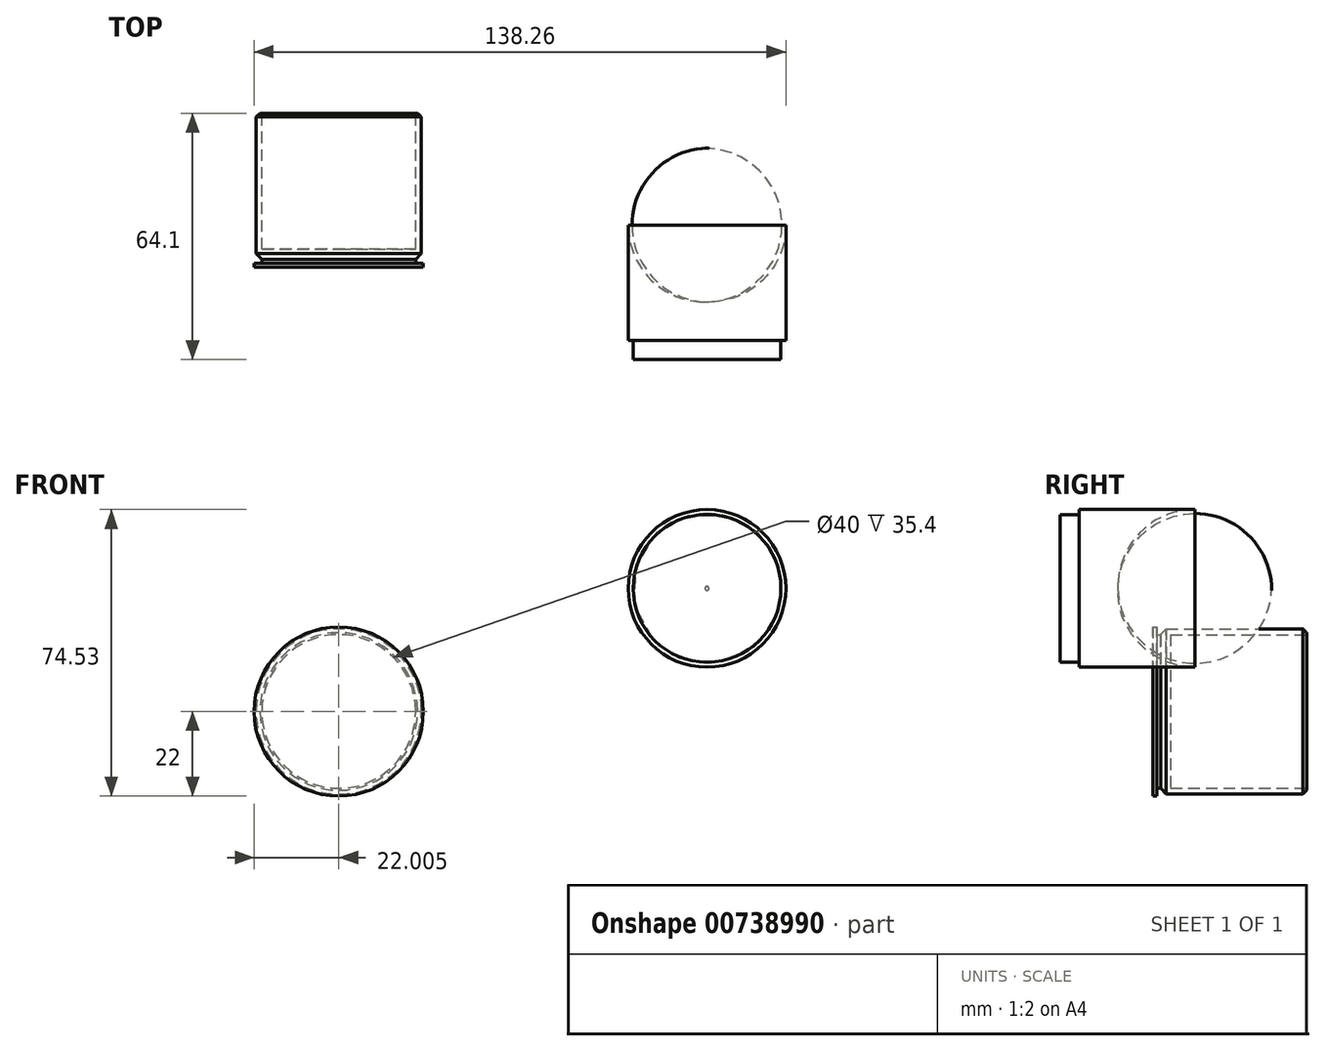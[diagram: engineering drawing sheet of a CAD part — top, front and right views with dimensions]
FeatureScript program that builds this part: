
annotation { "Feature Type Name" : "Feature", "Feature Type Description" : "" }
export const myFeature = defineFeature(function(context is Context, id is Id, definition is map)
    precondition{}
    {
        {
            var Q0;
            Q0=qCreatedBy(makeId("Top.planeOp"),FACE);
            var sketch = newSketch(context, id + "F0", { "sketchPlane" : qUnion([Q0])});
            skPoint(sketch, "E0", {"position": v(-36.63, 52.6) * mm});
            skPoint(sketch, "E1", {"position": v(-36.63, 22.6) * mm});
            skPoint(sketch, "E2", {"position": v(-38.13, 21.1) * mm});
            skPoint(sketch, "E3", {"position": v(-38.13, 20.1) * mm});
            skPoint(sketch, "E4", {"position": v(-36.13, 20.1) * mm});
            skPoint(sketch, "E5", {"position": v(-36.13, 19.1) * mm});
            skPoint(sketch, "E6", {"position": v(-38.13, 19.1) * mm});
            skPoint(sketch, "E7", {"position": v(-58.13, 19.1) * mm});
            skPoint(sketch, "E8", {"position": v(-58.13, 59.1) * mm});
            skLineSegment(sketch, "E9", {"start": v(-36.63, 52.6) * mm, "end": v(-36.63, 22.6) * mm});
            skLineSegment(sketch, "E10", {"start": v(-38.13, 21.1) * mm, "end": v(-38.13, 20.1) * mm});
            skLineSegment(sketch, "E11", {"start": v(-36.13, 20.1) * mm, "end": v(-38.13, 20.1) * mm});
            skLineSegment(sketch, "E12", {"start": v(-38.13, 21.1) * mm, "end": v(-36.63, 22.6) * mm});
            skLineSegment(sketch, "E13", {"start": v(-36.13, 20.1) * mm, "end": v(-36.13, 19.1) * mm});
            skLineSegment(sketch, "E14", {"start": v(-38.13, 19.1) * mm, "end": v(-58.13, 19.1) * mm});
            skLineSegment(sketch, "E15", {"start": v(-38.13, 19.1) * mm, "end": v(-36.13, 19.1) * mm});
            skLineSegment(sketch, "E16", {"start": v(-58.13, 59.1) * mm, "end": v(-58.13, 19.1) * mm});
            skPoint(sketch, "E17", {"position": v(-36.63, 59.1) * mm});
            skLineSegment(sketch, "E18", {"start": v(-58.13, 59.1) * mm, "end": v(-36.63, 59.1) * mm});
            skLineSegment(sketch, "E19", {"start": v(-36.63, 52.6) * mm, "end": v(-36.63, 59.1) * mm});
            skSolve(sketch);
        }
        {
            var Q0;
            Q0=qCreatedBy(makeId("Top.planeOp"),FACE);
            var sketch = newSketch(context, id + "F1", { "sketchPlane" : qUnion([Q0])});
            skLineSegment(sketch, "E20", {"start": v(-58.13, 59.1) * mm, "end": v(-58.13, 22.26) * mm});
            skSolve(sketch);
        }
        {
            var Q0;
            Q0=makeQuery(id+"F0.imprint","IMPRINT",FACE,{"disambiguationData":[TD([[makeQuery(id+"F0.imprint","IMPRINT",EDGE,{"derivedFrom":sQuery(id+"F0.wireOp",EDGE,"E10")}),-1.0]])]});
            var Q1;
            Q1=sQuery(id+"F1.wireOp",EDGE,"E20");
            revolve(context, id + "F2", {"surfaceOperationType" : NewSurfaceOperationType.NEW, "entities" : qUnion([Q0]), "axis" : qUnion([Q1]), "revolveType" : RevolveType.FULL});
        }
        {
            var Q0;
            Q0=makeQuery(id+"F2.opRevolve","SWEPT_FACE",FACE,{"disambiguationData":[OSD([sQuery(id+"F0.wireOp",EDGE,"E18")])]});
            var sketch = newSketch(context, id + "F3", { "sketchPlane" : qUnion([Q0])});
            skCircle(sketch, "E21", {"center": v(58.13, 0) * mm, "radius": 20 * mm});
            skSolve(sketch);
        }
        {
            var Q0;
            Q0=makeQuery(id+"F3.imprint","IMPRINT",FACE,{"disambiguationData":[TD([[makeQuery(id+"F3.imprint","IMPRINT",EDGE,{"derivedFrom":sQuery(id+"F3.wireOp",EDGE,"E21")}),1.0]])]});
            extrude(context, id + "F4", {"entities" : qUnion([Q0]), "operationType" : NewBodyOperationType.REMOVE, "oppositeDirection" : true, "depth" : 35.4 * mm, "offsetDistance" : 25 * mm});
        }
        {
            var Q0;
            Q0=makeQuery(id+"F2.opRevolve","SWEPT_EDGE",EDGE,{"disambiguationData":[OSD([sQuery(id+"F0.wireOp",EDGE,"E18"),sQuery(id+"F0.wireOp",EDGE,"E19")])]});
            chamfer(context, id + "F5", {"entities" : qUnion([Q0]), "width" : 1 * mm, "tangentPropagation" : true});
        }
        {
            var Q0;
            Q0=qCreatedBy(makeId("Front.planeOp"),FACE);
            var sketch = newSketch(context, id + "F6", { "sketchPlane" : qUnion([Q0])});
            skCircle(sketch, "E22", {"center": v(37.63, 32.03) * mm, "radius": 20.5 * mm});
            skSolve(sketch);
        }
        {
            var Q0;
            Q0 = qSketchRegion(id + "F6", true);
            extrude(context, id + "F7", {"entities" : qUnion([Q0]), "oppositeDirection" : true, "depth" : 50 * mm, "offsetDistance" : 25 * mm});
        }
        {
            var Q0;
            Q0=makeQuery(id+"F7.opExtrude","CAP_FACE",FACE,{"disambiguationData":[OSD([sQuery(id+"F6.wireOp",EDGE,"E22")])],"isStart":false});
            fillet(context, id + "F8", {"entities" : qUnion([Q0]), "radius" : 20 * mm, "tangentPropagation" : true, "allowEdgeOverflow" : false});
        }
        {
            var Q0;
            Q0=makeQuery(id+"F7.opExtrude","CAP_FACE",FACE,{"disambiguationData":[OSD([sQuery(id+"F6.wireOp",EDGE,"E22")])],"isStart":true});
            var sketch = newSketch(context, id + "F9", { "sketchPlane" : qUnion([Q0])});
            skCircle(sketch, "E23", {"center": v(37.63, 32.03) * mm, "radius": 19.22 * mm});
            skSolve(sketch);
        }
        {
            var Q0;
            Q0 = qSketchRegion(id + "F9", true);
            extrude(context, id + "F10", {"entities" : qUnion([Q0]), "operationType" : NewBodyOperationType.ADD, "depth" : 5 * mm, "offsetDistance" : 25 * mm});
        }
    });
